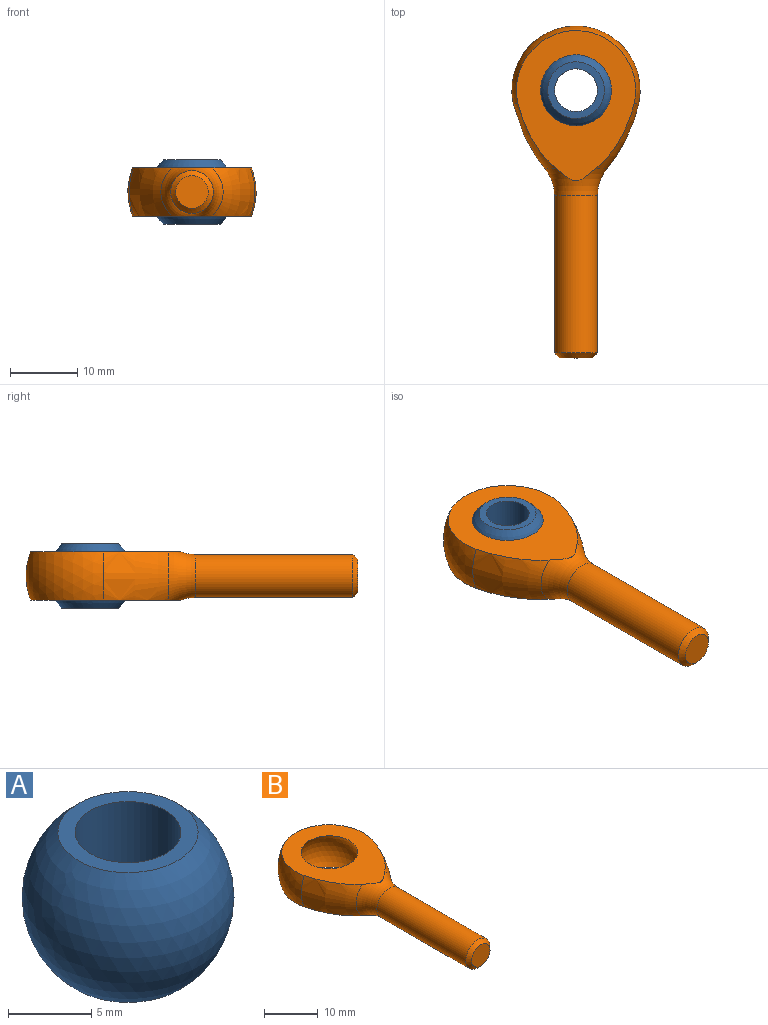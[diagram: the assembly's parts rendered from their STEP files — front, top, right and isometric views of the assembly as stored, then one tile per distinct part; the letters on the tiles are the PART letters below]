
ASSEMBLY  parts=2 mates=1
PART A: 4 faces, bbox 12.7x12.7x9.5 mm
  f0: cylinder r=3.17mm len=9.53mm, axis (0,0,-1), area 190mm2, adj f1,f3
  f1: plane 8.4x8.4mm, normal (0,0,-1), area 23.8mm2, adj f0,f2
  f2: sphere r=6.35mm, area 380mm2, adj f1,f3
  f3: plane 8.4x8.4mm, normal (0,0,1), area 23.8mm2, adj f0,f2
PART B: 10 faces, bbox 19.2x49.4x19.2 mm
  f0: torus R=9.53mm, axis (0,1,0), area 84.7mm2, adj f1,f2,f5,f6,f7
  f1: revolved ~14.4x9.62mm, area 81.1mm2, adj f0,f3,f6,f7
  f2: revolved ~14.4x9.62mm, area 81.1mm2, adj f0,f3,f6,f7
  f3: sphere r=9.53mm, area 243.1mm2, adj f1,f2,f6,f7
  f4: plane 4.83x4.83mm, normal (0,-1,0), area 18.3mm2, adj f9
  f5: cylinder r=3.17mm len=23.28mm, axis (0,1,0), area 464.5mm2, adj f0,f9
  f6: plane 22.26x17.66mm, normal (0,0,-1), area 201.3mm2, adj f0,f1,f2,f3,f8
  f7: plane 22.44x17.84mm, normal (0,0,1), area 201.3mm2, adj f0,f1,f2,f3,f8
  f8: sphere r=6.35mm, area 284.8mm2, adj f6,f7
  f9: cone r=3.17mm half-angle=45deg, axis (0,1,0), area 18.9mm2, adj f4,f5
PLACE A at identity
PLACE B at identity
MATE ball A.f0 <-> B.f3  axis (0,0,1) through (0,0,0)mm
